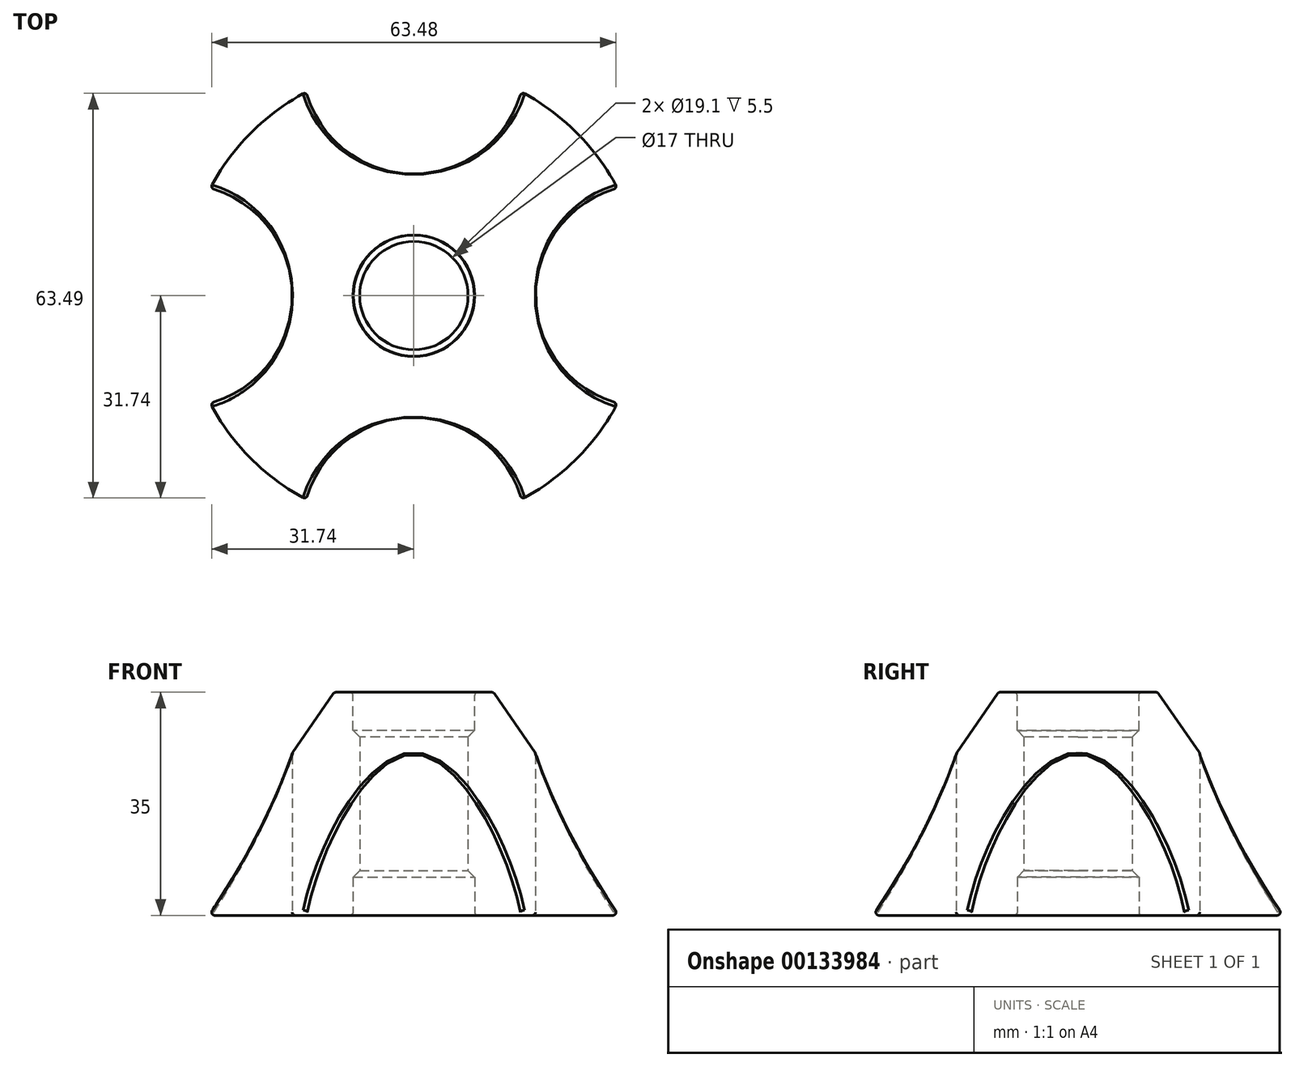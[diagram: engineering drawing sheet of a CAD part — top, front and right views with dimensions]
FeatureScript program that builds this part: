
annotation { "Feature Type Name" : "Feature", "Feature Type Description" : "" }
export const myFeature = defineFeature(function(context is Context, id is Id, definition is map)
    precondition{}
    {
        {
            var Q0;
            Q0=qCreatedBy(makeId("Top.planeOp"),FACE);
            var sketch = newSketch(context, id + "F0", { "sketchPlane" : qUnion([Q0])});
            skCircle(sketch, "E0", {"center": v(0, 0) * mm, "radius": 36.6 * mm});
            skSolve(sketch);
        }
        {
            var Q0;
            Q0=qCreatedBy(makeId("Top.planeOp"),FACE);
            cPlane(context, id + "F1", {"entities" : qUnion([Q0]), "cplaneType" : CPlaneType.OFFSET, "offset" : 35 * mm, "width" : 150 * mm, "height" : 150 * mm});
        }
        {
            var Q0;
            Q0=qCreatedBy(id+"F1.planeOp",FACE);
            var sketch = newSketch(context, id + "F2", { "sketchPlane" : qUnion([Q0])});
            skCircle(sketch, "E1", {"center": v(0, 0) * mm, "radius": 12.5 * mm});
            skSolve(sketch);
        }
        {
            var Q0;
            Q0=makeQuery(id+"F0.imprint","IMPRINT",FACE,{"disambiguationData":[TD([[makeQuery(id+"F0.imprint","IMPRINT",EDGE,{"derivedFrom":sQuery(id+"F0.wireOp",EDGE,"E0")}),1.0]])]});
            var Q1;
            Q1=makeQuery(id+"F2.imprint","IMPRINT",FACE,{"disambiguationData":[TD([[makeQuery(id+"F2.imprint","IMPRINT",EDGE,{"derivedFrom":sQuery(id+"F2.wireOp",EDGE,"E1")}),1.0]])]});
            loft(context, id + "F3", {"sheetProfilesArray" : [{ "sheetProfileEntities" : qUnion([Q0]) }, { "sheetProfileEntities" : qUnion([Q1]) }]});
        }
        {
            var Q0;
            Q0=makeQuery(id+"F3.opLoft","CAP_FACE",FACE,{"disambiguationData":[OSD([makeQuery(id+"F0.imprint","IMPRINT",FACE,{"disambiguationData":[TD([[makeQuery(id+"F0.imprint","IMPRINT",EDGE,{"derivedFrom":sQuery(id+"F0.wireOp",EDGE,"E0")}),1.0]])]})])],"isStart":true});
            var sketch = newSketch(context, id + "F4", { "sketchPlane" : qUnion([Q0])});
            skCircle(sketch, "E2", {"center": v(0, 0) * mm, "radius": 9.55 * mm});
            skSolve(sketch);
        }
        {
            var Q0;
            Q0 = qSketchRegion(id + "F4", true);
            extrude(context, id + "F5", {"entities" : qUnion([Q0]), "operationType" : NewBodyOperationType.REMOVE, "oppositeDirection" : true, "depth" : 6 * mm, "offsetDistance" : 25 * mm});
        }
        {
            var Q0;
            Q0=makeQuery(id+"F3.opLoft","CAP_FACE",FACE,{"disambiguationData":[OSD([makeQuery(id+"F2.imprint","IMPRINT",FACE,{"disambiguationData":[TD([[makeQuery(id+"F2.imprint","IMPRINT",EDGE,{"derivedFrom":sQuery(id+"F2.wireOp",EDGE,"E1")}),1.0]])]})])],"isStart":true});
            var sketch = newSketch(context, id + "F6", { "sketchPlane" : qUnion([Q0])});
            skCircle(sketch, "E3", {"center": v(0, 0) * mm, "radius": 9.55 * mm});
            skSolve(sketch);
        }
        {
            var Q0;
            Q0=makeQuery(id+"F6.imprint","IMPRINT",FACE,{"disambiguationData":[TD([[makeQuery(id+"F6.imprint","IMPRINT",EDGE,{"derivedFrom":sQuery(id+"F6.wireOp",EDGE,"E3")}),1.0]])]});
            extrude(context, id + "F7", {"entities" : qUnion([Q0]), "operationType" : NewBodyOperationType.REMOVE, "oppositeDirection" : true, "depth" : 6 * mm, "offsetDistance" : 25 * mm});
        }
        {
            var Q0;
            Q0=makeQuery(id+"F3.opLoft","CAP_FACE",FACE,{"disambiguationData":[OSD([makeQuery(id+"F0.imprint","IMPRINT",FACE,{"disambiguationData":[TD([[makeQuery(id+"F0.imprint","IMPRINT",EDGE,{"derivedFrom":sQuery(id+"F0.wireOp",EDGE,"E0")}),1.0]])]})])],"isStart":true});
            var sketch = newSketch(context, id + "F8", { "sketchPlane" : qUnion([Q0])});
            skCircle(sketch, "E4", {"center": v(0, 0) * mm, "radius": 8.5 * mm});
            skSolve(sketch);
        }
        {
            var Q0;
            Q0 = qSketchRegion(id + "F8", true);
            extrude(context, id + "F9", {"entities" : qUnion([Q0]), "operationType" : NewBodyOperationType.REMOVE, "endBound" : BoundingType.THROUGH_ALL, "oppositeDirection" : true, "depth" : 25 * mm, "offsetDistance" : 25 * mm});
        }
        {
            var Q0;
            Q0=makeQuery(id+"F3.opLoft","CAP_FACE",FACE,{"disambiguationData":[OSD([makeQuery(id+"F0.imprint","IMPRINT",FACE,{"disambiguationData":[TD([[makeQuery(id+"F0.imprint","IMPRINT",EDGE,{"derivedFrom":sQuery(id+"F0.wireOp",EDGE,"E0")}),1.0]])]})])],"isStart":true});
            var sketch = newSketch(context, id + "F10", { "sketchPlane" : qUnion([Q0])});
            skCircle(sketch, "E5", {"center": v(0, 36.6) * mm, "radius": 17.5 * mm});
            skCircle(sketch, "E6", {"center": v(36.6, 0) * mm, "radius": 17.5 * mm});
            skCircle(sketch, "E7", {"center": v(-0.01, -36.6) * mm, "radius": 17.5 * mm});
            skCircle(sketch, "E8", {"center": v(-36.6, 0) * mm, "radius": 17.5 * mm});
            skSolve(sketch);
        }
        {
            var Q0;
            Q0 = qSketchRegion(id + "F10", true);
            extrude(context, id + "F11", {"entities" : qUnion([Q0]), "operationType" : NewBodyOperationType.REMOVE, "endBound" : BoundingType.THROUGH_ALL, "oppositeDirection" : true, "depth" : 25 * mm, "offsetDistance" : 25 * mm});
        }
        {
            var Q0;
            Q0=makeQuery(id+"F3.opLoft","CAP_FACE",FACE,{"disambiguationData":[OSD([makeQuery(id+"F0.imprint","IMPRINT",FACE,{"disambiguationData":[TD([[makeQuery(id+"F0.imprint","IMPRINT",EDGE,{"derivedFrom":sQuery(id+"F0.wireOp",EDGE,"E0")}),1.0]])]})])],"isStart":true});
            var Q1;
            Q1=makeQuery(id+"F3.opLoft","CAP_FACE",FACE,{"disambiguationData":[OSD([makeQuery(id+"F2.imprint","IMPRINT",FACE,{"disambiguationData":[TD([[makeQuery(id+"F2.imprint","IMPRINT",EDGE,{"derivedFrom":sQuery(id+"F2.wireOp",EDGE,"E1")}),1.0]])]})])],"isStart":true});
            var Q2;
            Q2=makeQuery(id+"F11.boolean.opBoolean","COPY",FACE,{"derivedFrom":makeQuery(id+"F11.opExtrude","SWEPT_FACE",FACE,{"disambiguationData":[OSD([sQuery(id+"F10.wireOp",EDGE,"E6")])]})});
            var Q3;
            Q3=makeQuery(id+"F11.boolean.opBoolean","COPY",FACE,{"derivedFrom":makeQuery(id+"F11.opExtrude","SWEPT_FACE",FACE,{"disambiguationData":[OSD([sQuery(id+"F10.wireOp",EDGE,"E5")])]})});
            var Q4;
            Q4=makeQuery(id+"F11.boolean.opBoolean","COPY",FACE,{"derivedFrom":makeQuery(id+"F11.opExtrude","SWEPT_FACE",FACE,{"disambiguationData":[OSD([sQuery(id+"F10.wireOp",EDGE,"E8")])]})});
            var Q5;
            Q5=makeQuery(id+"F11.boolean.opBoolean","COPY",FACE,{"derivedFrom":makeQuery(id+"F11.opExtrude","SWEPT_FACE",FACE,{"disambiguationData":[OSD([sQuery(id+"F10.wireOp",EDGE,"E7")])]})});
            fillet(context, id + "F12", {"entities" : qUnion([Q0, Q1, Q2, Q3, Q4, Q5]), "radius" : 0.5 * mm, "tangentPropagation" : true, "allowEdgeOverflow" : false});
        }
        {
            var Q0;
            Q0=makeQuery(id+"F9.boolean.opBoolean","INTERSECT",EDGE,{"derivedFrom":[makeQuery(id+"F7.boolean.opBoolean","COPY",FACE,{"derivedFrom":makeQuery(id+"F7.opExtrude","CAP_FACE",FACE,{"disambiguationData":[OSD([sQuery(id+"F6.wireOp",EDGE,"E3")])],"isStart":false})}),makeQuery(id+"F9.opExtrude","SWEPT_FACE",FACE,{"disambiguationData":[OSD([sQuery(id+"F8.wireOp",EDGE,"E4")])]})]});
            var Q1;
            Q1=makeQuery(id+"F9.boolean.opBoolean","INTERSECT",EDGE,{"derivedFrom":[makeQuery(id+"F5.boolean.opBoolean","COPY",FACE,{"derivedFrom":makeQuery(id+"F5.opExtrude","CAP_FACE",FACE,{"disambiguationData":[OSD([sQuery(id+"F4.wireOp",EDGE,"E2")])],"isStart":false})}),makeQuery(id+"F9.opExtrude","SWEPT_FACE",FACE,{"disambiguationData":[OSD([sQuery(id+"F8.wireOp",EDGE,"E4")])]})]});
            chamfer(context, id + "F13", {"entities" : qUnion([Q0, Q1]), "width" : 1 * mm, "tangentPropagation" : true});
        }
    });
